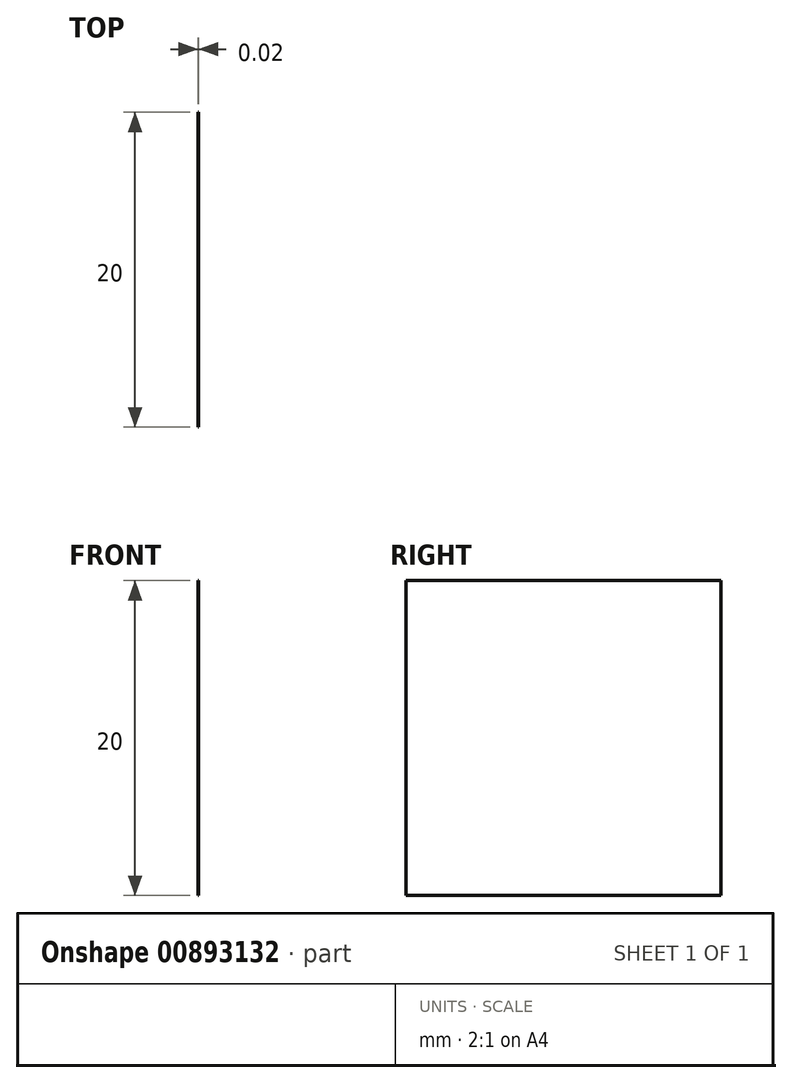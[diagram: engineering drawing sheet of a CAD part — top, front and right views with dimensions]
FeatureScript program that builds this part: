
annotation { "Feature Type Name" : "Feature", "Feature Type Description" : "" }
export const myFeature = defineFeature(function(context is Context, id is Id, definition is map)
    precondition{}
    {
        {
            var Q0;
            Q0=qCreatedBy(makeId("Right.planeOp"),FACE);
            var sketch = newSketch(context, id + "F0", { "sketchPlane" : qUnion([Q0])});
            skLineSegment(sketch, "E0.bottom", {"start": v(0, 0) * mm, "end": v(20, 0) * mm});
            skLineSegment(sketch, "E0.top", {"start": v(0, -20) * mm, "end": v(20, -20) * mm});
            skLineSegment(sketch, "E0.left", {"start": v(0, 0) * mm, "end": v(0, -20) * mm});
            skLineSegment(sketch, "E0.right", {"start": v(20, 0) * mm, "end": v(20, -20) * mm});
            skSolve(sketch);
        }
        {
            var Q0;
            Q0=makeQuery(id+"F0.imprint","IMPRINT",FACE,{"disambiguationData":[TD([[makeQuery(id+"F0.imprint","IMPRINT",EDGE,{"derivedFrom":sQuery(id+"F0.wireOp",EDGE,"E0.bottom")}),-1.0]])]});
            extrude(context, id + "F1", {"entities" : qUnion([Q0]), "depth" : 0.01 * mm, "offsetDistance" : 25 * mm});
        }
    });
